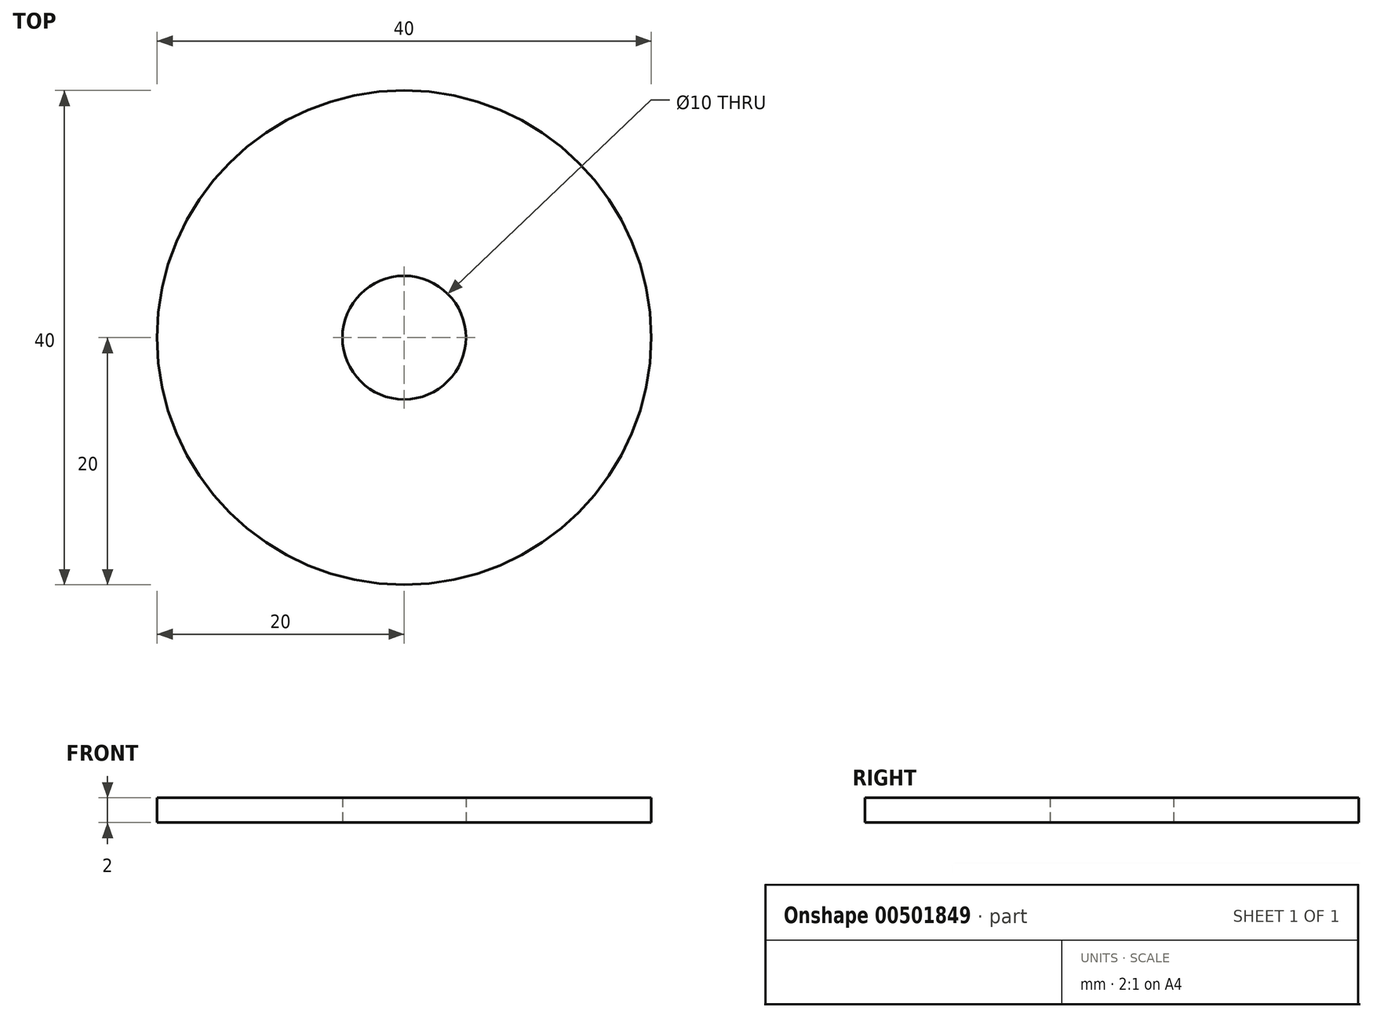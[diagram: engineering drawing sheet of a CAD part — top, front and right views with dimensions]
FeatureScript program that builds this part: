
annotation { "Feature Type Name" : "Feature", "Feature Type Description" : "" }
export const myFeature = defineFeature(function(context is Context, id is Id, definition is map)
    precondition{}
    {
        {
            var Q0;
            Q0=qCreatedBy(makeId("Top.planeOp"),FACE);
            var sketch = newSketch(context, id + "F0", { "sketchPlane" : qUnion([Q0])});
            skCircle(sketch, "E0", {"center": v(0, 0) * mm, "radius": 20 * mm});
            skCircle(sketch, "E1", {"center": v(0, 0) * mm, "radius": 5 * mm});
            skSolve(sketch);
        }
        {
            var Q0;
            Q0 = qSketchRegion(id + "F0", true);
            extrude(context, id + "F1", {"entities" : qUnion([Q0]), "depth" : 2 * mm});
        }
    });
